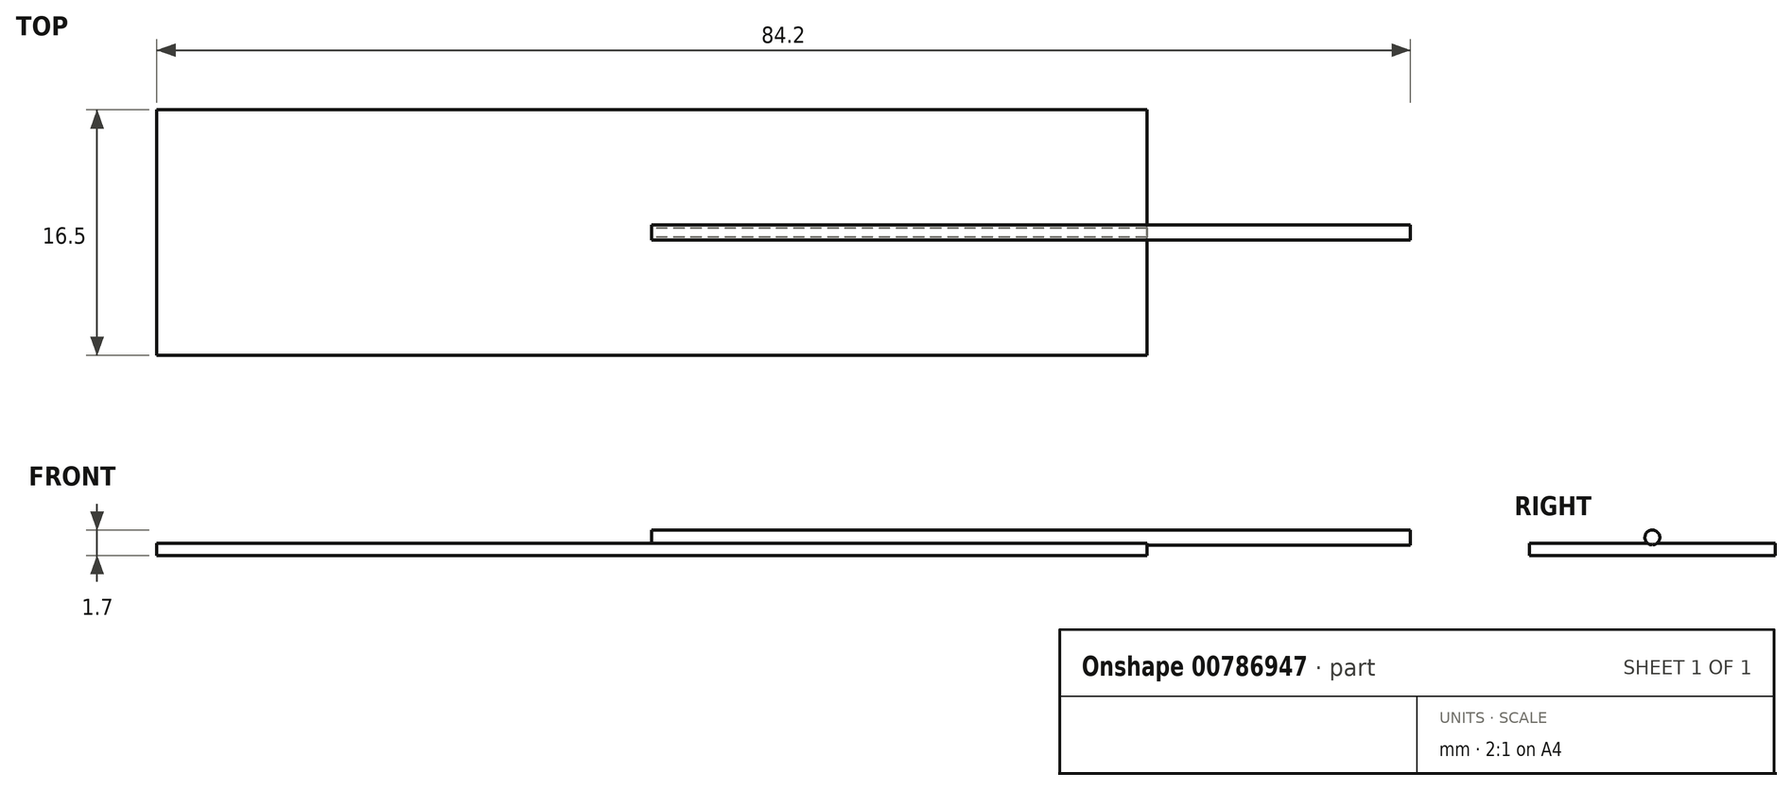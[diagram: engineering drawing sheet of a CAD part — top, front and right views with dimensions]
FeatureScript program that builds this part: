
annotation { "Feature Type Name" : "Feature", "Feature Type Description" : "" }
export const myFeature = defineFeature(function(context is Context, id is Id, definition is map)
    precondition{}
    {
        {
            var Q0;
            Q0=qCreatedBy(makeId("Top.planeOp"),FACE);
            var sketch = newSketch(context, id + "F0", { "sketchPlane" : qUnion([Q0])});
            skLineSegment(sketch, "E0.bottom", {"start": v(0, 0) * mm, "end": v(66.5, 0) * mm});
            skLineSegment(sketch, "E0.top", {"start": v(0, 16.5) * mm, "end": v(66.5, 16.5) * mm});
            skLineSegment(sketch, "E0.left", {"start": v(0, 0) * mm, "end": v(0, 16.5) * mm});
            skLineSegment(sketch, "E0.right", {"start": v(66.5, 0) * mm, "end": v(66.5, 16.5) * mm});
            skSolve(sketch);
        }
        {
            var Q0;
            Q0 = qSketchRegion(id + "F0", true);
            extrude(context, id + "F1", {"entities" : qUnion([Q0]), "depth" : 0.8 * mm, "offsetDistance" : 25 * mm});
        }
        {
            var Q0;
            Q0=makeQuery(id+"F1.opExtrude","SWEPT_FACE",FACE,{"disambiguationData":[OSD([sQuery(id+"F0.wireOp",EDGE,"E0.right")])]});
            var sketch = newSketch(context, id + "F2", { "sketchPlane" : qUnion([Q0])});
            skCircle(sketch, "E1", {"center": v(8.25, 1.2) * mm, "radius": 0.5 * mm});
            skPoint(sketch, "E1.centerSnap0", {"position": v(8.25, 0.8) * mm});
            skSolve(sketch);
        }
        {
            var Q0;
            Q0 = qSketchRegion(id + "F2", true);
            extrude(context, id + "F3", {"entities" : qUnion([Q0]), "operationType" : NewBodyOperationType.ADD, "depth" : 17.7 * mm, "offsetDistance" : 25 * mm, "hasSecondDirection" : true, "secondDirectionOppositeDirection" : true, "secondDirectionDepth" : (66.5 / 2) * mm});
        }
    });
